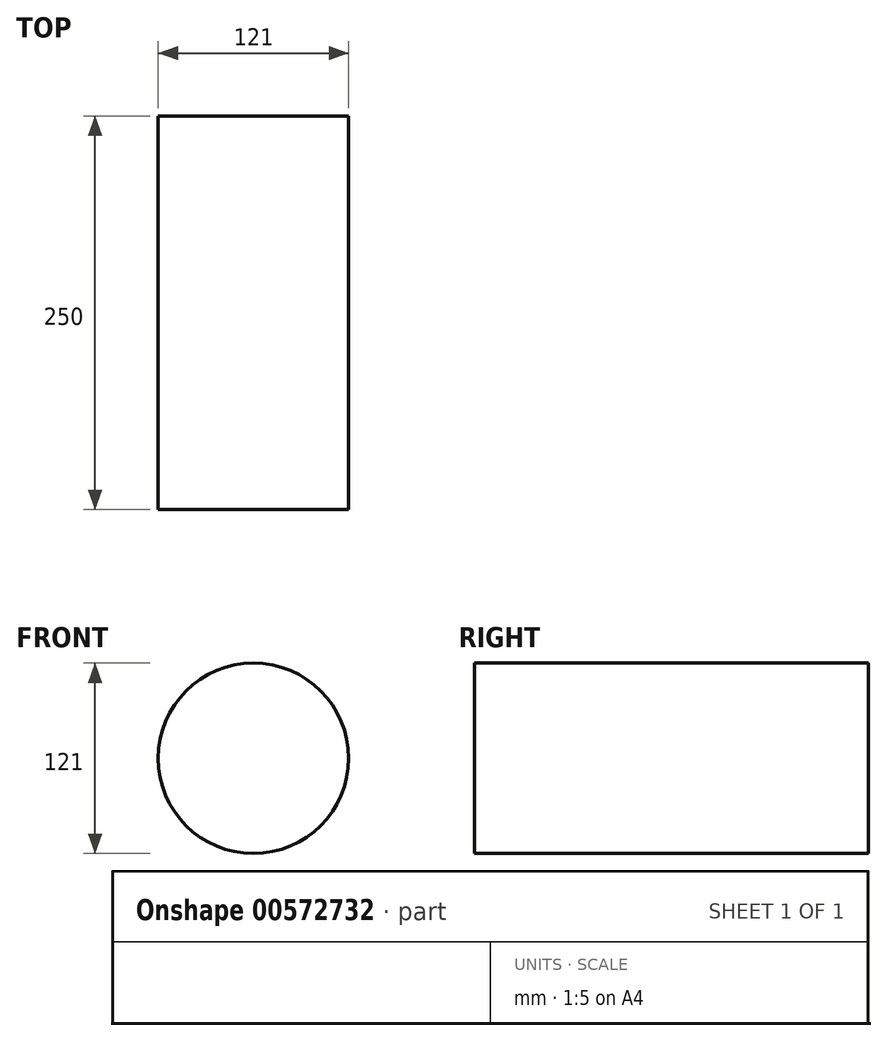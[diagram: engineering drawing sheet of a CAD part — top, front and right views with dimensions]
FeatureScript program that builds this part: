
annotation { "Feature Type Name" : "Feature", "Feature Type Description" : "" }
export const myFeature = defineFeature(function(context is Context, id is Id, definition is map)
    precondition{}
    {
        {
            var Q0;
            Q0=qCreatedBy(makeId("Front.planeOp"),FACE);
            var sketch = newSketch(context, id + "F0", { "sketchPlane" : qUnion([Q0])});
            skCircle(sketch, "E0", {"center": v(0, 0) * mm, "radius": 60.5 * mm});
            skSolve(sketch);
        }
        {
            var Q0;
            Q0=makeQuery(id+"F0.imprint","IMPRINT",FACE,{"disambiguationData":[TD([[makeQuery(id+"F0.imprint","IMPRINT",EDGE,{"derivedFrom":sQuery(id+"F0.wireOp",EDGE,"E0")}),1.0]])]});
            extrude(context, id + "F1", {"entities" : qUnion([Q0]), "depth" : 250 * mm, "offsetDistance" : 25 * mm});
        }
    });
